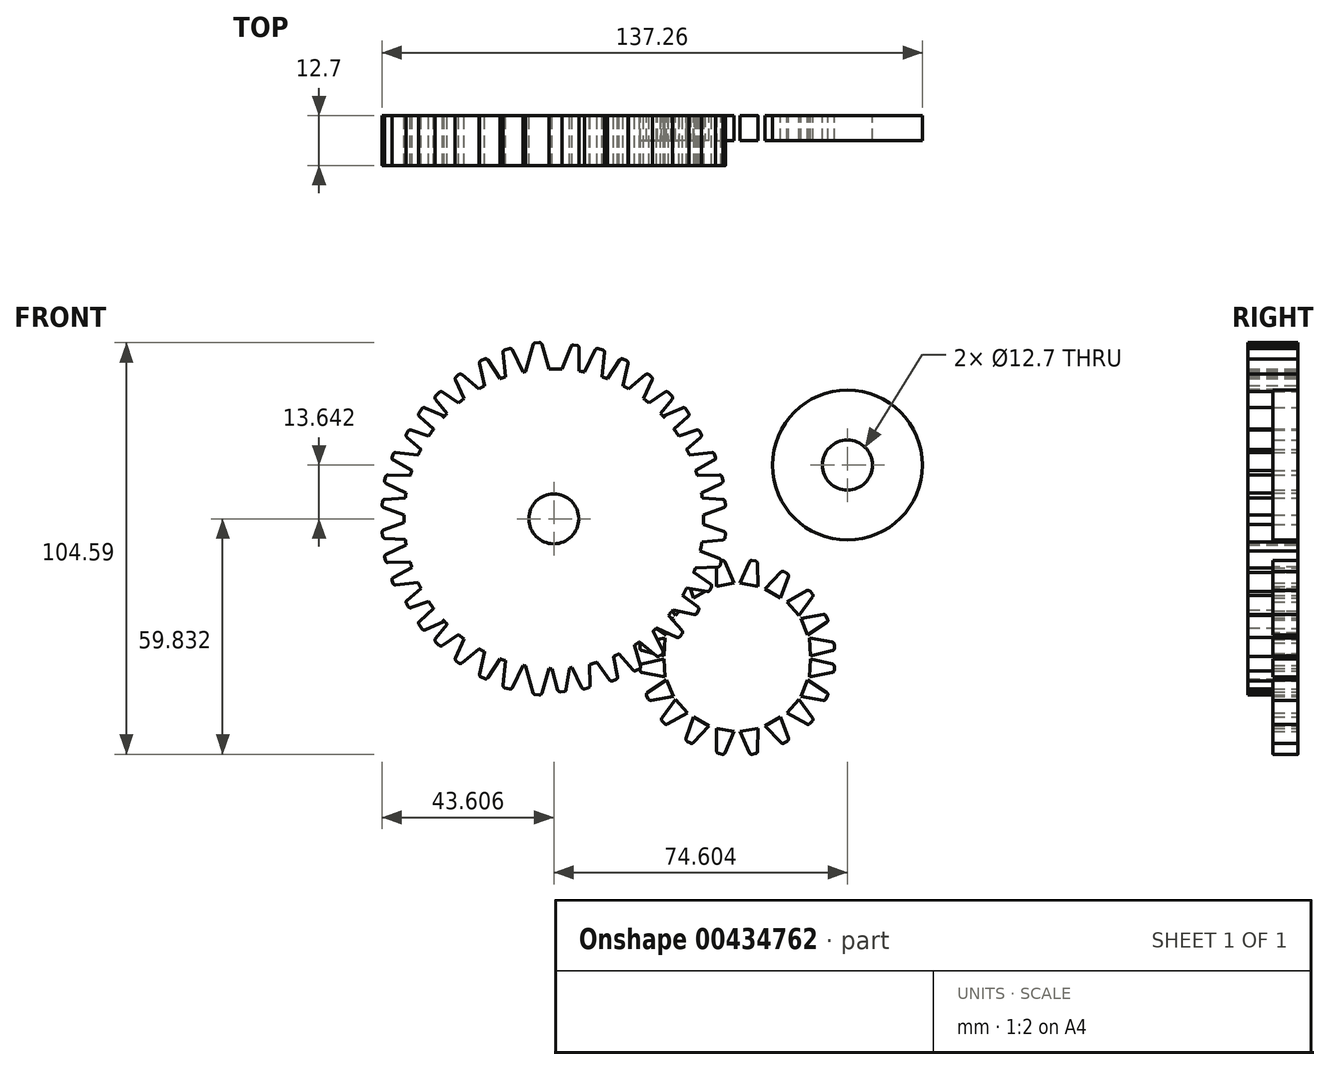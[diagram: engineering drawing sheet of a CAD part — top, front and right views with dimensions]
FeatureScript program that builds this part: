
annotation { "Feature Type Name" : "Feature", "Feature Type Description" : "" }
export const myFeature = defineFeature(function(context is Context, id is Id, definition is map)
    precondition{}
    {
        {
            var Q0;
            Q0=qCreatedBy(makeId("Front.planeOp"),FACE);
            var sketch = newSketch(context, id + "F0", { "sketchPlane" : qUnion([Q0])});
            skCircle(sketch, "E0", {"center": v(-46.58, 35.21) * mm, "radius": 38.1 * mm});
            skCircle(sketch, "E1", {"center": v(-46.58, 35.21) * mm, "radius": 6.35 * mm});
            skLineSegment(sketch, "E2", {"start": v(-46.58, -6.11) * mm, "end": v(-46.58, 81.19) * mm});
            skLineSegment(sketch, "E3", {"start": v(-89.25, 35.21) * mm, "end": v(4.56, 35.21) * mm});
            skSolve(sketch);
        }
        {
            var Q0;
            Q0 = qSketchRegion(id + "F0", true);
            extrude(context, id + "F1", {"entities" : qUnion([Q0]), "depth" : 12.7 * mm});
        }
        {
            var Q0;
            Q0=qCreatedBy(makeId("Front.planeOp"),FACE);
            var sketch = newSketch(context, id + "F2", { "sketchPlane" : qUnion([Q0])});
            skCircle(sketch, "E4", {"center": v(28.02, 48.85) * mm, "radius": 19.05 * mm});
            skCircle(sketch, "E5", {"center": v(28.02, 48.85) * mm, "radius": 6.35 * mm});
            skLineSegment(sketch, "E6", {"start": v(28.02, 28) * mm, "end": v(28.02, 72.6) * mm});
            skLineSegment(sketch, "E7", {"start": v(7.02, 48.85) * mm, "end": v(52.13, 48.85) * mm});
            skLineSegment(sketch, "E8", {"start": v(-5.28, 18.03) * mm, "end": v(-5.2, 23.83) * mm});
            skLineSegment(sketch, "E9", {"start": v(-4.68, 24.44) * mm, "end": v(-3.77, 24.6) * mm});
            skLineSegment(sketch, "E10", {"start": v(-3.08, 24.23) * mm, "end": v(-0.77, 18.85) * mm});
            skLineSegment(sketch, "E11", {"start": v(-5.28, 18.03) * mm, "end": v(-0.77, 18.85) * mm});
            skArc(sketch, "E12.filletArc", {"start": v(-4.68, 24.44) * mm, "mid": v(-5.05, 24.23) * mm, "end": v(-5.2, 23.83) * mm});
            skArc(sketch, "E13.filletArc", {"start": v(-3.08, 24.23) * mm, "mid": v(-3.36, 24.54) * mm, "end": v(-3.77, 24.6) * mm});
            skLineSegment(sketch, "E14.0", {"start": v(-5.28, 18.03) * mm, "end": v(-0.77, 18.85) * mm, "construction": true});
            skLineSegment(sketch, "E15", {"start": v(-11.07, 15.08) * mm, "end": v(-12.98, 20.55) * mm});
            skLineSegment(sketch, "E16", {"start": v(-12.7, 21.31) * mm, "end": v(-11.9, 21.78) * mm});
            skLineSegment(sketch, "E17", {"start": v(-11.12, 21.66) * mm, "end": v(-7.1, 17.4) * mm});
            skLineSegment(sketch, "E18", {"start": v(-11.07, 15.08) * mm, "end": v(-7.1, 17.4) * mm});
            skArc(sketch, "E19.filletArc", {"start": v(-12.7, 21.31) * mm, "mid": v(-12.97, 20.98) * mm, "end": v(-12.98, 20.55) * mm});
            skArc(sketch, "E20.filletArc", {"start": v(-11.12, 21.66) * mm, "mid": v(-11.5, 21.86) * mm, "end": v(-11.9, 21.78) * mm});
            skLineSegment(sketch, "E21.0", {"start": v(-11.07, 15.08) * mm, "end": v(-7.1, 17.4) * mm, "construction": true});
            skLineSegment(sketch, "E22", {"start": v(-18.58, 0.36) * mm, "end": v(-24.22, 1.72) * mm});
            skLineSegment(sketch, "E23", {"start": v(-24.7, 2.37) * mm, "end": v(-24.66, 3.28) * mm});
            skLineSegment(sketch, "E24", {"start": v(-24.15, 3.88) * mm, "end": v(-18.39, 4.95) * mm});
            skLineSegment(sketch, "E25", {"start": v(-18.58, 0.36) * mm, "end": v(-18.39, 4.95) * mm});
            skArc(sketch, "E26.filletArc", {"start": v(-24.7, 2.37) * mm, "mid": v(-24.58, 1.96) * mm, "end": v(-24.22, 1.72) * mm});
            skArc(sketch, "E27.filletArc", {"start": v(-24.15, 3.88) * mm, "mid": v(-24.5, 3.67) * mm, "end": v(-24.66, 3.28) * mm});
            skLineSegment(sketch, "E28.0", {"start": v(-18.58, 0.36) * mm, "end": v(-18.39, 4.95) * mm, "construction": true});
            skLineSegment(sketch, "E29", {"start": v(-17.91, 5.67) * mm, "end": v(-22.74, 8.88) * mm});
            skLineSegment(sketch, "E30", {"start": v(-22.98, 9.65) * mm, "end": v(-22.63, 10.5) * mm});
            skLineSegment(sketch, "E31", {"start": v(-21.93, 10.88) * mm, "end": v(-16.16, 9.91) * mm});
            skLineSegment(sketch, "E32", {"start": v(-17.91, 5.67) * mm, "end": v(-16.16, 9.91) * mm});
            skArc(sketch, "E33.filletArc", {"start": v(-22.98, 9.65) * mm, "mid": v(-23, 9.22) * mm, "end": v(-22.74, 8.88) * mm});
            skArc(sketch, "E34.filletArc", {"start": v(-21.93, 10.88) * mm, "mid": v(-22.35, 10.8) * mm, "end": v(-22.63, 10.5) * mm});
            skLineSegment(sketch, "E35.0", {"start": v(-17.91, 5.67) * mm, "end": v(-16.16, 9.91) * mm, "construction": true});
            skLineSegment(sketch, "E36", {"start": v(-15.7, 10.67) * mm, "end": v(-19.14, 15.34) * mm});
            skLineSegment(sketch, "E37", {"start": v(-19.1, 16.14) * mm, "end": v(-18.47, 16.82) * mm});
            skLineSegment(sketch, "E38", {"start": v(-17.7, 16.95) * mm, "end": v(-12.6, 14.06) * mm});
            skLineSegment(sketch, "E39", {"start": v(-15.7, 10.67) * mm, "end": v(-12.6, 14.06) * mm});
            skArc(sketch, "E40.filletArc", {"start": v(-19.1, 16.14) * mm, "mid": v(-19.26, 15.75) * mm, "end": v(-19.14, 15.34) * mm});
            skArc(sketch, "E41.filletArc", {"start": v(-17.7, 16.95) * mm, "mid": v(-18.1, 17.02) * mm, "end": v(-18.47, 16.82) * mm});
            skLineSegment(sketch, "E42.0", {"start": v(-15.7, 10.67) * mm, "end": v(-12.6, 14.06) * mm, "construction": true});
            skLineSegment(sketch, "E43.MirrorCS", {"start": v(5.28, 18.03) * mm, "end": v(0.77, 18.85) * mm, "construction": true});
            skLineSegment(sketch, "E44.MirrorCS", {"start": v(5.28, 18.03) * mm, "end": v(5.2, 23.83) * mm});
            skArc(sketch, "E45.MirrorCS", {"start": v(4.68, 24.44) * mm, "mid": v(5.05, 24.23) * mm, "end": v(5.2, 23.83) * mm});
            skLineSegment(sketch, "E46.MirrorCS", {"start": v(4.68, 24.44) * mm, "end": v(3.77, 24.6) * mm});
            skArc(sketch, "E47.MirrorCS", {"start": v(3.08, 24.23) * mm, "mid": v(3.36, 24.54) * mm, "end": v(3.77, 24.6) * mm});
            skLineSegment(sketch, "E48.MirrorCS", {"start": v(3.08, 24.23) * mm, "end": v(0.77, 18.85) * mm});
            skLineSegment(sketch, "E49.MirrorCS", {"start": v(11.07, 15.08) * mm, "end": v(7.1, 17.4) * mm, "construction": true});
            skLineSegment(sketch, "E50.MirrorCS", {"start": v(11.07, 15.08) * mm, "end": v(12.98, 20.55) * mm});
            skArc(sketch, "E51.MirrorCS", {"start": v(12.7, 21.31) * mm, "mid": v(12.97, 20.98) * mm, "end": v(12.98, 20.55) * mm});
            skLineSegment(sketch, "E52.MirrorCS", {"start": v(12.7, 21.31) * mm, "end": v(11.9, 21.78) * mm});
            skArc(sketch, "E53.MirrorCS", {"start": v(11.12, 21.66) * mm, "mid": v(11.5, 21.86) * mm, "end": v(11.9, 21.78) * mm});
            skLineSegment(sketch, "E54.MirrorCS", {"start": v(11.12, 21.66) * mm, "end": v(7.1, 17.4) * mm});
            skLineSegment(sketch, "E55.MirrorCS", {"start": v(15.7, 10.67) * mm, "end": v(12.6, 14.06) * mm, "construction": true});
            skLineSegment(sketch, "E56.MirrorCS", {"start": v(15.7, 10.67) * mm, "end": v(19.14, 15.34) * mm});
            skLineSegment(sketch, "E57.MirrorCS", {"start": v(19.1, 16.14) * mm, "end": v(18.47, 16.82) * mm});
            skArc(sketch, "E58.MirrorCS", {"start": v(17.7, 16.95) * mm, "mid": v(18.1, 17.02) * mm, "end": v(18.47, 16.82) * mm});
            skLineSegment(sketch, "E59.MirrorCS", {"start": v(17.7, 16.95) * mm, "end": v(12.6, 14.06) * mm});
            skLineSegment(sketch, "E60.MirrorCS", {"start": v(17.91, 5.67) * mm, "end": v(16.16, 9.91) * mm, "construction": true});
            skLineSegment(sketch, "E61.MirrorCS", {"start": v(17.91, 5.67) * mm, "end": v(22.74, 8.88) * mm});
            skArc(sketch, "E62.MirrorCS", {"start": v(22.98, 9.65) * mm, "mid": v(23, 9.22) * mm, "end": v(22.74, 8.88) * mm});
            skLineSegment(sketch, "E63.MirrorCS", {"start": v(22.98, 9.65) * mm, "end": v(22.63, 10.5) * mm});
            skArc(sketch, "E64.MirrorCS", {"start": v(21.93, 10.88) * mm, "mid": v(22.35, 10.8) * mm, "end": v(22.63, 10.5) * mm});
            skLineSegment(sketch, "E65.MirrorCS", {"start": v(21.93, 10.88) * mm, "end": v(16.16, 9.91) * mm});
            skArc(sketch, "E66.MirrorCS", {"start": v(19.1, 16.14) * mm, "mid": v(19.26, 15.75) * mm, "end": v(19.14, 15.34) * mm});
            skLineSegment(sketch, "E67.MirrorCS", {"start": v(18.58, 0.36) * mm, "end": v(18.39, 4.95) * mm, "construction": true});
            skLineSegment(sketch, "E68.MirrorCS", {"start": v(18.58, 0.36) * mm, "end": v(24.22, 1.72) * mm});
            skArc(sketch, "E69.MirrorCS", {"start": v(24.7, 2.37) * mm, "mid": v(24.58, 1.96) * mm, "end": v(24.22, 1.72) * mm});
            skLineSegment(sketch, "E70.MirrorCS", {"start": v(24.7, 2.37) * mm, "end": v(24.66, 3.28) * mm});
            skArc(sketch, "E71.MirrorCS", {"start": v(24.15, 3.88) * mm, "mid": v(24.5, 3.67) * mm, "end": v(24.66, 3.28) * mm});
            skLineSegment(sketch, "E72.MirrorCS", {"start": v(24.15, 3.88) * mm, "end": v(18.39, 4.95) * mm});
            skLineSegment(sketch, "E73.MirrorCS", {"start": v(5.28, -18.03) * mm, "end": v(0.77, -18.85) * mm, "construction": true});
            skLineSegment(sketch, "E74.MirrorCS", {"start": v(3.08, -24.23) * mm, "end": v(0.77, -18.85) * mm});
            skArc(sketch, "E75.MirrorCS", {"start": v(3.08, -24.23) * mm, "mid": v(3.36, -24.54) * mm, "end": v(3.77, -24.6) * mm});
            skLineSegment(sketch, "E76.MirrorCS", {"start": v(4.68, -24.44) * mm, "end": v(3.77, -24.6) * mm});
            skArc(sketch, "E77.MirrorCS", {"start": v(4.68, -24.44) * mm, "mid": v(5.05, -24.23) * mm, "end": v(5.2, -23.83) * mm});
            skLineSegment(sketch, "E78.MirrorCS", {"start": v(5.28, -18.03) * mm, "end": v(5.2, -23.83) * mm});
            skLineSegment(sketch, "E79.MirrorCS", {"start": v(11.07, -15.08) * mm, "end": v(7.1, -17.4) * mm, "construction": true});
            skLineSegment(sketch, "E80.MirrorCS", {"start": v(11.12, -21.66) * mm, "end": v(7.1, -17.4) * mm});
            skArc(sketch, "E81.MirrorCS", {"start": v(11.12, -21.66) * mm, "mid": v(11.5, -21.86) * mm, "end": v(11.9, -21.78) * mm});
            skLineSegment(sketch, "E82.MirrorCS", {"start": v(12.7, -21.31) * mm, "end": v(11.9, -21.78) * mm});
            skArc(sketch, "E83.MirrorCS", {"start": v(12.7, -21.31) * mm, "mid": v(12.97, -20.98) * mm, "end": v(12.98, -20.55) * mm});
            skLineSegment(sketch, "E84.MirrorCS", {"start": v(11.07, -15.08) * mm, "end": v(12.98, -20.55) * mm});
            skLineSegment(sketch, "E85.MirrorCS", {"start": v(15.7, -10.67) * mm, "end": v(12.6, -14.06) * mm, "construction": true});
            skLineSegment(sketch, "E86.MirrorCS", {"start": v(17.7, -16.95) * mm, "end": v(12.6, -14.06) * mm});
            skArc(sketch, "E87.MirrorCS", {"start": v(17.7, -16.95) * mm, "mid": v(18.1, -17.02) * mm, "end": v(18.47, -16.82) * mm});
            skLineSegment(sketch, "E88.MirrorCS", {"start": v(19.1, -16.14) * mm, "end": v(18.47, -16.82) * mm});
            skArc(sketch, "E89.MirrorCS", {"start": v(19.1, -16.14) * mm, "mid": v(19.26, -15.75) * mm, "end": v(19.14, -15.34) * mm});
            skLineSegment(sketch, "E90.MirrorCS", {"start": v(15.7, -10.67) * mm, "end": v(19.14, -15.34) * mm});
            skLineSegment(sketch, "E91.MirrorCS", {"start": v(17.91, -5.67) * mm, "end": v(16.16, -9.91) * mm, "construction": true});
            skLineSegment(sketch, "E92.MirrorCS", {"start": v(21.93, -10.88) * mm, "end": v(16.16, -9.91) * mm});
            skArc(sketch, "E93.MirrorCS", {"start": v(21.93, -10.88) * mm, "mid": v(22.35, -10.8) * mm, "end": v(22.63, -10.5) * mm});
            skLineSegment(sketch, "E94.MirrorCS", {"start": v(22.98, -9.65) * mm, "end": v(22.63, -10.5) * mm});
            skArc(sketch, "E95.MirrorCS", {"start": v(22.98, -9.65) * mm, "mid": v(23, -9.22) * mm, "end": v(22.74, -8.88) * mm});
            skLineSegment(sketch, "E96.MirrorCS", {"start": v(17.91, -5.67) * mm, "end": v(22.74, -8.88) * mm});
            skLineSegment(sketch, "E97.MirrorCS", {"start": v(18.58, -0.36) * mm, "end": v(18.39, -4.95) * mm, "construction": true});
            skLineSegment(sketch, "E98.MirrorCS", {"start": v(18.58, -0.36) * mm, "end": v(24.22, -1.72) * mm});
            skArc(sketch, "E99.MirrorCS", {"start": v(24.7, -2.37) * mm, "mid": v(24.58, -1.96) * mm, "end": v(24.22, -1.72) * mm});
            skLineSegment(sketch, "E100.MirrorCS", {"start": v(24.7, -2.37) * mm, "end": v(24.66, -3.28) * mm});
            skArc(sketch, "E101.MirrorCS", {"start": v(24.15, -3.88) * mm, "mid": v(24.5, -3.67) * mm, "end": v(24.66, -3.28) * mm});
            skLineSegment(sketch, "E102.MirrorCS", {"start": v(24.15, -3.88) * mm, "end": v(18.39, -4.95) * mm});
            skLineSegment(sketch, "E103.MirrorCS", {"start": v(-18.58, -0.36) * mm, "end": v(-24.22, -1.72) * mm});
            skArc(sketch, "E104.MirrorCS", {"start": v(-24.7, -2.37) * mm, "mid": v(-24.58, -1.96) * mm, "end": v(-24.22, -1.72) * mm});
            skLineSegment(sketch, "E105.MirrorCS", {"start": v(-24.7, -2.37) * mm, "end": v(-24.66, -3.28) * mm});
            skArc(sketch, "E106.MirrorCS", {"start": v(-24.15, -3.88) * mm, "mid": v(-24.5, -3.67) * mm, "end": v(-24.66, -3.28) * mm});
            skLineSegment(sketch, "E107.MirrorCS", {"start": v(-24.15, -3.88) * mm, "end": v(-18.39, -4.95) * mm});
            skLineSegment(sketch, "E108.MirrorCS", {"start": v(-18.58, -0.36) * mm, "end": v(-18.39, -4.95) * mm, "construction": true});
            skLineSegment(sketch, "E109.MirrorCS", {"start": v(-17.91, -5.67) * mm, "end": v(-16.16, -9.91) * mm, "construction": true});
            skLineSegment(sketch, "E110.MirrorCS", {"start": v(-17.91, -5.67) * mm, "end": v(-22.74, -8.88) * mm});
            skArc(sketch, "E111.MirrorCS", {"start": v(-22.98, -9.65) * mm, "mid": v(-23, -9.22) * mm, "end": v(-22.74, -8.88) * mm});
            skLineSegment(sketch, "E112.MirrorCS", {"start": v(-22.98, -9.65) * mm, "end": v(-22.63, -10.5) * mm});
            skArc(sketch, "E113.MirrorCS", {"start": v(-21.93, -10.88) * mm, "mid": v(-22.35, -10.8) * mm, "end": v(-22.63, -10.5) * mm});
            skLineSegment(sketch, "E114.MirrorCS", {"start": v(-21.93, -10.88) * mm, "end": v(-16.16, -9.91) * mm});
            skLineSegment(sketch, "E115.MirrorCS", {"start": v(-15.7, -10.67) * mm, "end": v(-12.6, -14.06) * mm, "construction": true});
            skLineSegment(sketch, "E116.MirrorCS", {"start": v(-15.7, -10.67) * mm, "end": v(-19.14, -15.34) * mm});
            skArc(sketch, "E117.MirrorCS", {"start": v(-19.1, -16.14) * mm, "mid": v(-19.26, -15.75) * mm, "end": v(-19.14, -15.34) * mm});
            skLineSegment(sketch, "E118.MirrorCS", {"start": v(-19.1, -16.14) * mm, "end": v(-18.47, -16.82) * mm});
            skArc(sketch, "E119.MirrorCS", {"start": v(-17.7, -16.95) * mm, "mid": v(-18.1, -17.02) * mm, "end": v(-18.47, -16.82) * mm});
            skLineSegment(sketch, "E120.MirrorCS", {"start": v(-17.7, -16.95) * mm, "end": v(-12.6, -14.06) * mm});
            skLineSegment(sketch, "E121.MirrorCS", {"start": v(-11.07, -15.08) * mm, "end": v(-7.1, -17.4) * mm, "construction": true});
            skLineSegment(sketch, "E122.MirrorCS", {"start": v(-11.07, -15.08) * mm, "end": v(-12.98, -20.55) * mm});
            skLineSegment(sketch, "E123.MirrorCS", {"start": v(-12.7, -21.31) * mm, "end": v(-11.9, -21.78) * mm});
            skArc(sketch, "E124.MirrorCS", {"start": v(-12.7, -21.31) * mm, "mid": v(-12.97, -20.98) * mm, "end": v(-12.98, -20.55) * mm});
            skArc(sketch, "E125.MirrorCS", {"start": v(-11.12, -21.66) * mm, "mid": v(-11.5, -21.86) * mm, "end": v(-11.9, -21.78) * mm});
            skLineSegment(sketch, "E126.MirrorCS", {"start": v(-11.12, -21.66) * mm, "end": v(-7.1, -17.4) * mm});
            skLineSegment(sketch, "E127.MirrorCS", {"start": v(-5.28, -18.03) * mm, "end": v(-0.77, -18.85) * mm, "construction": true});
            skLineSegment(sketch, "E128.MirrorCS", {"start": v(-5.28, -18.03) * mm, "end": v(-5.2, -23.83) * mm});
            skArc(sketch, "E129.MirrorCS", {"start": v(-4.68, -24.44) * mm, "mid": v(-5.05, -24.23) * mm, "end": v(-5.2, -23.83) * mm});
            skLineSegment(sketch, "E130.MirrorCS", {"start": v(-4.68, -24.44) * mm, "end": v(-3.77, -24.6) * mm});
            skArc(sketch, "E131.MirrorCS", {"start": v(-3.08, -24.23) * mm, "mid": v(-3.36, -24.54) * mm, "end": v(-3.77, -24.6) * mm});
            skLineSegment(sketch, "E132.MirrorCS", {"start": v(-3.08, -24.23) * mm, "end": v(-0.77, -18.85) * mm});
            skLineSegment(sketch, "E133", {"start": v(-18.39, -4.95) * mm, "end": v(-18.58, -0.36) * mm});
            skLineSegment(sketch, "E134", {"start": v(-16.16, -9.91) * mm, "end": v(-17.91, -5.67) * mm});
            skLineSegment(sketch, "E135", {"start": v(-12.6, -14.06) * mm, "end": v(-15.7, -10.67) * mm});
            skLineSegment(sketch, "E136", {"start": v(-7.1, -17.4) * mm, "end": v(-11.07, -15.08) * mm});
            skLineSegment(sketch, "E137", {"start": v(-0.77, -18.85) * mm, "end": v(-5.28, -18.03) * mm});
            skLineSegment(sketch, "E138", {"start": v(5.28, -18.03) * mm, "end": v(0.77, -18.85) * mm});
            skLineSegment(sketch, "E139", {"start": v(11.07, -15.08) * mm, "end": v(7.1, -17.4) * mm});
            skLineSegment(sketch, "E140", {"start": v(15.7, -10.67) * mm, "end": v(12.6, -14.06) * mm});
            skLineSegment(sketch, "E141", {"start": v(17.91, -5.67) * mm, "end": v(16.16, -9.91) * mm});
            skLineSegment(sketch, "E142", {"start": v(18.39, -4.95) * mm, "end": v(18.58, -0.36) * mm});
            skLineSegment(sketch, "E143", {"start": v(18.58, 0.36) * mm, "end": v(18.39, 4.95) * mm});
            skLineSegment(sketch, "E144", {"start": v(17.91, 5.67) * mm, "end": v(16.16, 9.91) * mm});
            skLineSegment(sketch, "E145", {"start": v(15.7, 10.67) * mm, "end": v(12.6, 14.06) * mm});
            skLineSegment(sketch, "E146", {"start": v(11.07, 15.08) * mm, "end": v(7.1, 17.4) * mm});
            skLineSegment(sketch, "E147", {"start": v(5.28, 18.03) * mm, "end": v(0.77, 18.85) * mm});
            skSolve(sketch);
        }
        {
            var Q0;
            Q0 = qSketchRegion(id + "F2", true);
            extrude(context, id + "F3", {"entities" : qUnion([Q0]), "depth" : 6.35 * mm});
        }
        {
            var Q0;
            Q0=qCreatedBy(makeId("Front.planeOp"),FACE);
            var sketch = newSketch(context, id + "F4", { "sketchPlane" : qUnion([Q0])});
            skLineSegment(sketch, "E148", {"start": v(-53.8, 72.63) * mm, "end": v(-51.9, 79.41) * mm});
            skLineSegment(sketch, "E149", {"start": v(-51.34, 79.87) * mm, "end": v(-50.28, 79.96) * mm});
            skLineSegment(sketch, "E150", {"start": v(-49.62, 79.5) * mm, "end": v(-47.8, 73.16) * mm});
            skLineSegment(sketch, "E151", {"start": v(-53.8, 72.63) * mm, "end": v(-47.8, 73.16) * mm});
            skPoint(sketch, "E152.visualSharp", {"position": v(-51.78, 79.83) * mm});
            skArc(sketch, "E152.filletArc", {"start": v(-51.34, 79.87) * mm, "mid": v(-51.7, 79.73) * mm, "end": v(-51.9, 79.41) * mm});
            skPoint(sketch, "E153.visualSharp", {"position": v(-49.76, 80.01) * mm});
            skArc(sketch, "E153.filletArc", {"start": v(-49.62, 79.5) * mm, "mid": v(-49.87, 79.86) * mm, "end": v(-50.28, 79.96) * mm});
            skLineSegment(sketch, "E154", {"start": v(-44.47, 73.21) * mm, "end": v(-42.23, 79) * mm});
            skLineSegment(sketch, "E155", {"start": v(-41.53, 79.4) * mm, "end": v(-40.69, 79.25) * mm});
            skLineSegment(sketch, "E156", {"start": v(-40.16, 78.63) * mm, "end": v(-40.16, 72.45) * mm});
            skLineSegment(sketch, "E157", {"start": v(-44.47, 73.21) * mm, "end": v(-40.16, 72.45) * mm});
            skArc(sketch, "E158.filletArc", {"start": v(-41.53, 79.4) * mm, "mid": v(-41.95, 79.33) * mm, "end": v(-42.23, 79) * mm});
            skArc(sketch, "E159.filletArc", {"start": v(-40.16, 78.63) * mm, "mid": v(-40.31, 79.04) * mm, "end": v(-40.69, 79.25) * mm});
            skLineSegment(sketch, "E160.0", {"start": v(-44.47, 73.21) * mm, "end": v(-40.16, 72.45) * mm, "construction": true});
            skLineSegment(sketch, "E161", {"start": v(-38.87, 72.35) * mm, "end": v(-36.07, 78.1) * mm});
            skLineSegment(sketch, "E162", {"start": v(-35.34, 78.44) * mm, "end": v(-34.13, 78.12) * mm});
            skLineSegment(sketch, "E163", {"start": v(-33.66, 77.44) * mm, "end": v(-34.37, 71.16) * mm});
            skLineSegment(sketch, "E164", {"start": v(-38.87, 72.35) * mm, "end": v(-34.37, 71.16) * mm});
            skArc(sketch, "E165.filletArc", {"start": v(-35.34, 78.44) * mm, "mid": v(-35.76, 78.4) * mm, "end": v(-36.07, 78.1) * mm});
            skArc(sketch, "E166.filletArc", {"start": v(-33.66, 77.44) * mm, "mid": v(-33.77, 77.87) * mm, "end": v(-34.13, 78.12) * mm});
            skLineSegment(sketch, "E167.0", {"start": v(-38.87, 72.35) * mm, "end": v(-34.37, 71.16) * mm, "construction": true});
            skLineSegment(sketch, "E168", {"start": v(-33.08, 70.6) * mm, "end": v(-29.83, 75.58) * mm});
            skLineSegment(sketch, "E169", {"start": v(-29.06, 75.82) * mm, "end": v(-28.14, 75.45) * mm});
            skLineSegment(sketch, "E170", {"start": v(-27.76, 74.73) * mm, "end": v(-29.04, 68.96) * mm});
            skLineSegment(sketch, "E171", {"start": v(-33.08, 70.6) * mm, "end": v(-29.04, 68.96) * mm});
            skArc(sketch, "E172.filletArc", {"start": v(-29.06, 75.82) * mm, "mid": v(-29.49, 75.84) * mm, "end": v(-29.83, 75.58) * mm});
            skArc(sketch, "E173.filletArc", {"start": v(-27.76, 74.73) * mm, "mid": v(-27.82, 75.16) * mm, "end": v(-28.14, 75.45) * mm});
            skLineSegment(sketch, "E174.0", {"start": v(-33.08, 70.6) * mm, "end": v(-29.04, 68.96) * mm, "construction": true});
            skLineSegment(sketch, "E175", {"start": v(-27.74, 68.12) * mm, "end": v(-23.24, 71.82) * mm});
            skLineSegment(sketch, "E176", {"start": v(-22.43, 71.82) * mm, "end": v(-21.78, 71.29) * mm});
            skLineSegment(sketch, "E177", {"start": v(-21.61, 70.53) * mm, "end": v(-24.06, 65.31) * mm});
            skLineSegment(sketch, "E178", {"start": v(-27.74, 68.12) * mm, "end": v(-24.06, 65.31) * mm});
            skArc(sketch, "E179.filletArc", {"start": v(-22.43, 71.82) * mm, "mid": v(-22.83, 71.97) * mm, "end": v(-23.24, 71.82) * mm});
            skArc(sketch, "E180.filletArc", {"start": v(-21.61, 70.53) * mm, "mid": v(-21.57, 70.94) * mm, "end": v(-21.78, 71.29) * mm});
            skLineSegment(sketch, "E181", {"start": v(-22.64, 64.39) * mm, "end": v(-18.3, 67.4) * mm});
            skLineSegment(sketch, "E182", {"start": v(-17.5, 67.33) * mm, "end": v(-16.58, 66.44) * mm});
            skLineSegment(sketch, "E183", {"start": v(-16.54, 65.58) * mm, "end": v(-19.82, 61.65) * mm});
            skLineSegment(sketch, "E184", {"start": v(-22.64, 64.39) * mm, "end": v(-19.82, 61.65) * mm});
            skArc(sketch, "E185.filletArc", {"start": v(-17.5, 67.33) * mm, "mid": v(-17.89, 67.5) * mm, "end": v(-18.3, 67.4) * mm});
            skArc(sketch, "E186.filletArc", {"start": v(-16.54, 65.58) * mm, "mid": v(-16.4, 66.02) * mm, "end": v(-16.58, 66.44) * mm});
            skLineSegment(sketch, "E187.0", {"start": v(-22.64, 64.39) * mm, "end": v(-19.82, 61.65) * mm, "construction": true});
            skLineSegment(sketch, "E188", {"start": v(-12.27, 51.4) * mm, "end": v(-6.43, 52.03) * mm});
            skLineSegment(sketch, "E189", {"start": v(-5.75, 51.59) * mm, "end": v(-5.52, 50.84) * mm});
            skLineSegment(sketch, "E190", {"start": v(-5.82, 50.1) * mm, "end": v(-11, 47.3) * mm});
            skLineSegment(sketch, "E191", {"start": v(-12.27, 51.4) * mm, "end": v(-11, 47.3) * mm});
            skArc(sketch, "E192.filletArc", {"start": v(-5.75, 51.59) * mm, "mid": v(-6.01, 51.93) * mm, "end": v(-6.43, 52.03) * mm});
            skArc(sketch, "E193.filletArc", {"start": v(-5.82, 50.1) * mm, "mid": v(-5.54, 50.41) * mm, "end": v(-5.52, 50.84) * mm});
            skLineSegment(sketch, "E194.0", {"start": v(-12.27, 51.4) * mm, "end": v(-11, 47.3) * mm, "construction": true});
            skLineSegment(sketch, "E195", {"start": v(-10.26, 46.18) * mm, "end": v(-4.47, 46.32) * mm});
            skLineSegment(sketch, "E196", {"start": v(-3.83, 45.83) * mm, "end": v(-3.63, 44.93) * mm});
            skLineSegment(sketch, "E197", {"start": v(-3.98, 44.22) * mm, "end": v(-9.27, 41.7) * mm});
            skLineSegment(sketch, "E198", {"start": v(-10.26, 46.18) * mm, "end": v(-9.27, 41.7) * mm});
            skArc(sketch, "E199.filletArc", {"start": v(-3.83, 45.83) * mm, "mid": v(-4.06, 46.2) * mm, "end": v(-4.47, 46.32) * mm});
            skArc(sketch, "E200.filletArc", {"start": v(-3.98, 44.22) * mm, "mid": v(-3.68, 44.52) * mm, "end": v(-3.63, 44.93) * mm});
            skLineSegment(sketch, "E201.0", {"start": v(-10.26, 46.18) * mm, "end": v(-9.27, 41.7) * mm, "construction": true});
            skLineSegment(sketch, "E202", {"start": v(-15.38, 56.07) * mm, "end": v(-10.36, 57.79) * mm});
            skLineSegment(sketch, "E203", {"start": v(-9.6, 57.5) * mm, "end": v(-9.15, 56.72) * mm});
            skLineSegment(sketch, "E204", {"start": v(-9.29, 55.93) * mm, "end": v(-13.62, 52.15) * mm});
            skLineSegment(sketch, "E205", {"start": v(-15.38, 56.07) * mm, "end": v(-13.62, 52.15) * mm});
            skArc(sketch, "E206.filletArc", {"start": v(-9.6, 57.5) * mm, "mid": v(-9.93, 57.78) * mm, "end": v(-10.36, 57.79) * mm});
            skArc(sketch, "E207.filletArc", {"start": v(-9.29, 55.93) * mm, "mid": v(-9.08, 56.3) * mm, "end": v(-9.15, 56.72) * mm});
            skLineSegment(sketch, "E208", {"start": v(-9.48, 40.53) * mm, "end": v(-3.7, 40.16) * mm});
            skLineSegment(sketch, "E209", {"start": v(-3.1, 39.61) * mm, "end": v(-2.99, 38.7) * mm});
            skLineSegment(sketch, "E210", {"start": v(-3.4, 38.02) * mm, "end": v(-8.88, 35.97) * mm});
            skLineSegment(sketch, "E211", {"start": v(-9.48, 40.53) * mm, "end": v(-8.88, 35.97) * mm});
            skArc(sketch, "E212.filletArc", {"start": v(-3.1, 39.61) * mm, "mid": v(-3.3, 40) * mm, "end": v(-3.7, 40.16) * mm});
            skArc(sketch, "E213.filletArc", {"start": v(-3.4, 38.02) * mm, "mid": v(-3.07, 38.3) * mm, "end": v(-2.99, 38.7) * mm});
            skLineSegment(sketch, "E214.0", {"start": v(-9.48, 40.53) * mm, "end": v(-8.88, 35.97) * mm, "construction": true});
            skLineSegment(sketch, "E215", {"start": v(-31.54, 0.77) * mm, "end": v(-30.39, -4.91) * mm});
            skLineSegment(sketch, "E216", {"start": v(-30.77, -5.62) * mm, "end": v(-31.62, -5.98) * mm});
            skLineSegment(sketch, "E217", {"start": v(-32.38, -5.76) * mm, "end": v(-35.78, -0.99) * mm});
            skLineSegment(sketch, "E218", {"start": v(-31.54, 0.77) * mm, "end": v(-35.78, -0.99) * mm});
            skArc(sketch, "E219.filletArc", {"start": v(-30.77, -5.62) * mm, "mid": v(-30.45, -5.34) * mm, "end": v(-30.39, -4.91) * mm});
            skArc(sketch, "E220.filletArc", {"start": v(-32.38, -5.76) * mm, "mid": v(-32.03, -6) * mm, "end": v(-31.62, -5.98) * mm});
            skLineSegment(sketch, "E221.0", {"start": v(-31.54, 0.77) * mm, "end": v(-35.78, -0.99) * mm, "construction": true});
            skLineSegment(sketch, "E222", {"start": v(-37.55, -1.37) * mm, "end": v(-37.4, -7.16) * mm});
            skLineSegment(sketch, "E223", {"start": v(-37.9, -7.8) * mm, "end": v(-38.8, -8) * mm});
            skLineSegment(sketch, "E224", {"start": v(-39.5, -7.65) * mm, "end": v(-42.03, -2.36) * mm});
            skLineSegment(sketch, "E225", {"start": v(-37.55, -1.37) * mm, "end": v(-42.03, -2.36) * mm});
            skArc(sketch, "E226.filletArc", {"start": v(-37.9, -7.8) * mm, "mid": v(-37.54, -7.57) * mm, "end": v(-37.4, -7.16) * mm});
            skArc(sketch, "E227.filletArc", {"start": v(-39.5, -7.65) * mm, "mid": v(-39.21, -7.95) * mm, "end": v(-38.8, -8) * mm});
            skLineSegment(sketch, "E228.0", {"start": v(-37.55, -1.37) * mm, "end": v(-42.03, -2.36) * mm, "construction": true});
            skLineSegment(sketch, "E229", {"start": v(-26.2, 3.38) * mm, "end": v(-24.55, -2.18) * mm});
            skLineSegment(sketch, "E230", {"start": v(-24.87, -2.93) * mm, "end": v(-25.68, -3.35) * mm});
            skLineSegment(sketch, "E231", {"start": v(-26.46, -3.2) * mm, "end": v(-30.26, 1.26) * mm});
            skLineSegment(sketch, "E232", {"start": v(-26.2, 3.38) * mm, "end": v(-30.26, 1.26) * mm});
            skArc(sketch, "E233.filletArc", {"start": v(-24.87, -2.93) * mm, "mid": v(-24.58, -2.61) * mm, "end": v(-24.55, -2.18) * mm});
            skArc(sketch, "E234.filletArc", {"start": v(-26.46, -3.2) * mm, "mid": v(-26.1, -3.41) * mm, "end": v(-25.68, -3.35) * mm});
            skLineSegment(sketch, "E235.0", {"start": v(-26.2, 3.38) * mm, "end": v(-30.26, 1.26) * mm, "construction": true});
            skLineSegment(sketch, "E236", {"start": v(-21.42, 6.87) * mm, "end": v(-18.84, 1.68) * mm});
            skLineSegment(sketch, "E237", {"start": v(-19.02, 0.9) * mm, "end": v(-19.75, 0.33) * mm});
            skLineSegment(sketch, "E238", {"start": v(-20.54, 0.35) * mm, "end": v(-25.06, 4.08) * mm});
            skLineSegment(sketch, "E239", {"start": v(-21.42, 6.87) * mm, "end": v(-25.06, 4.08) * mm});
            skArc(sketch, "E240.filletArc", {"start": v(-19.02, 0.9) * mm, "mid": v(-18.79, 1.25) * mm, "end": v(-18.84, 1.68) * mm});
            skArc(sketch, "E241.filletArc", {"start": v(-20.54, 0.35) * mm, "mid": v(-20.15, 0.2) * mm, "end": v(-19.75, 0.33) * mm});
            skLineSegment(sketch, "E242.0", {"start": v(-21.42, 6.87) * mm, "end": v(-25.06, 4.08) * mm, "construction": true});
            skLineSegment(sketch, "E243", {"start": v(-17.86, 11.17) * mm, "end": v(-14.03, 6.82) * mm});
            skLineSegment(sketch, "E244", {"start": v(-14, 6.02) * mm, "end": v(-14.56, 5.29) * mm});
            skLineSegment(sketch, "E245", {"start": v(-15.33, 5.1) * mm, "end": v(-20.65, 7.53) * mm});
            skLineSegment(sketch, "E246", {"start": v(-17.86, 11.17) * mm, "end": v(-20.65, 7.53) * mm});
            skArc(sketch, "E247.filletArc", {"start": v(-14, 6.02) * mm, "mid": v(-13.87, 6.42) * mm, "end": v(-14.03, 6.82) * mm});
            skArc(sketch, "E248.filletArc", {"start": v(-15.33, 5.1) * mm, "mid": v(-14.9, 5.06) * mm, "end": v(-14.56, 5.29) * mm});
            skLineSegment(sketch, "E249.0", {"start": v(-17.86, 11.17) * mm, "end": v(-20.65, 7.53) * mm, "construction": true});
            skLineSegment(sketch, "E250", {"start": v(-14.66, 16.28) * mm, "end": v(-10, 12.83) * mm});
            skLineSegment(sketch, "E251", {"start": v(-9.8, 12.05) * mm, "end": v(-10.2, 11.22) * mm});
            skLineSegment(sketch, "E252", {"start": v(-10.9, 10.87) * mm, "end": v(-16.63, 12.13) * mm});
            skLineSegment(sketch, "E253", {"start": v(-14.66, 16.28) * mm, "end": v(-16.63, 12.13) * mm});
            skArc(sketch, "E254.filletArc", {"start": v(-9.8, 12.05) * mm, "mid": v(-9.76, 12.48) * mm, "end": v(-10, 12.83) * mm});
            skArc(sketch, "E255.filletArc", {"start": v(-10.9, 10.87) * mm, "mid": v(-10.49, 10.92) * mm, "end": v(-10.2, 11.22) * mm});
            skLineSegment(sketch, "E256.0", {"start": v(-14.66, 16.28) * mm, "end": v(-16.63, 12.13) * mm, "construction": true});
            skLineSegment(sketch, "E257", {"start": v(-11.6, 21.91) * mm, "end": v(-6.78, 18.7) * mm});
            skLineSegment(sketch, "E258", {"start": v(-6.54, 17.93) * mm, "end": v(-6.9, 17.09) * mm});
            skLineSegment(sketch, "E259", {"start": v(-7.59, 16.7) * mm, "end": v(-13.36, 17.67) * mm});
            skLineSegment(sketch, "E260", {"start": v(-11.6, 21.91) * mm, "end": v(-13.36, 17.67) * mm});
            skArc(sketch, "E261.filletArc", {"start": v(-6.54, 17.93) * mm, "mid": v(-6.52, 18.36) * mm, "end": v(-6.78, 18.7) * mm});
            skArc(sketch, "E262.filletArc", {"start": v(-7.59, 16.7) * mm, "mid": v(-7.17, 16.77) * mm, "end": v(-6.9, 17.09) * mm});
            skLineSegment(sketch, "E263.0", {"start": v(-11.6, 21.91) * mm, "end": v(-13.36, 17.67) * mm, "construction": true});
            skLineSegment(sketch, "E264", {"start": v(-9.92, 27.21) * mm, "end": v(-4.52, 25.12) * mm});
            skLineSegment(sketch, "E265", {"start": v(-4.12, 24.42) * mm, "end": v(-4.28, 23.51) * mm});
            skLineSegment(sketch, "E266", {"start": v(-4.88, 23) * mm, "end": v(-10.73, 22.7) * mm});
            skLineSegment(sketch, "E267", {"start": v(-9.92, 27.21) * mm, "end": v(-10.73, 22.7) * mm});
            skArc(sketch, "E268.filletArc", {"start": v(-4.12, 24.42) * mm, "mid": v(-4.2, 24.84) * mm, "end": v(-4.52, 25.12) * mm});
            skArc(sketch, "E269.filletArc", {"start": v(-4.88, 23) * mm, "mid": v(-4.49, 23.15) * mm, "end": v(-4.28, 23.51) * mm});
            skLineSegment(sketch, "E270.0", {"start": v(-9.92, 27.21) * mm, "end": v(-10.73, 22.7) * mm, "construction": true});
            skLineSegment(sketch, "E271", {"start": v(-8.89, 33.84) * mm, "end": v(-3.4, 32) * mm});
            skLineSegment(sketch, "E272", {"start": v(-2.97, 31.31) * mm, "end": v(-3.09, 30.4) * mm});
            skLineSegment(sketch, "E273", {"start": v(-3.66, 29.85) * mm, "end": v(-9.49, 29.3) * mm});
            skLineSegment(sketch, "E274", {"start": v(-8.89, 33.84) * mm, "end": v(-9.49, 29.3) * mm});
            skArc(sketch, "E275.filletArc", {"start": v(-2.97, 31.31) * mm, "mid": v(-3.06, 31.73) * mm, "end": v(-3.4, 32) * mm});
            skArc(sketch, "E276.filletArc", {"start": v(-3.66, 29.85) * mm, "mid": v(-3.27, 30.03) * mm, "end": v(-3.09, 30.4) * mm});
            skLineSegment(sketch, "E277.0", {"start": v(-8.89, 33.84) * mm, "end": v(-9.49, 29.3) * mm, "construction": true});
            skLineSegment(sketch, "E278.0", {"start": v(-53.8, 72.63) * mm, "end": v(-47.8, 73.16) * mm, "construction": true});
            skLineSegment(sketch, "E279", {"start": v(-18.7, 61.28) * mm, "end": v(-13.87, 63.4) * mm});
            skLineSegment(sketch, "E280", {"start": v(-13.1, 63.18) * mm, "end": v(-12.33, 62.08) * mm});
            skLineSegment(sketch, "E281", {"start": v(-12.43, 61.24) * mm, "end": v(-16.3, 57.82) * mm});
            skLineSegment(sketch, "E282", {"start": v(-18.7, 61.28) * mm, "end": v(-16.3, 57.82) * mm});
            skArc(sketch, "E283.filletArc", {"start": v(-13.1, 63.18) * mm, "mid": v(-13.44, 63.43) * mm, "end": v(-13.87, 63.4) * mm});
            skArc(sketch, "E284.filletArc", {"start": v(-12.43, 61.24) * mm, "mid": v(-12.22, 61.64) * mm, "end": v(-12.33, 62.08) * mm});
            skLineSegment(sketch, "E285.0", {"start": v(-18.7, 61.28) * mm, "end": v(-16.3, 57.82) * mm, "construction": true});
            skLineSegment(sketch, "E286.MirrorCS", {"start": v(-54.3, 72.35) * mm, "end": v(-57.1, 78.1) * mm});
            skLineSegment(sketch, "E287.MirrorCS", {"start": v(-54.3, 72.35) * mm, "end": v(-58.8, 71.16) * mm, "construction": true});
            skLineSegment(sketch, "E288.MirrorCS", {"start": v(-59.5, 77.44) * mm, "end": v(-58.8, 71.16) * mm});
            skLineSegment(sketch, "E289.MirrorCS", {"start": v(-57.83, 78.44) * mm, "end": v(-59.04, 78.12) * mm});
            skArc(sketch, "E290.MirrorCS", {"start": v(-57.83, 78.44) * mm, "mid": v(-57.4, 78.4) * mm, "end": v(-57.1, 78.1) * mm});
            skArc(sketch, "E291.MirrorCS", {"start": v(-59.5, 77.44) * mm, "mid": v(-59.4, 77.87) * mm, "end": v(-59.04, 78.12) * mm});
            skLineSegment(sketch, "E292.MirrorCS", {"start": v(-60.09, 70.6) * mm, "end": v(-64.13, 68.96) * mm, "construction": true});
            skLineSegment(sketch, "E293.MirrorCS", {"start": v(-65.4, 74.73) * mm, "end": v(-64.13, 68.96) * mm});
            skArc(sketch, "E294.MirrorCS", {"start": v(-65.4, 74.73) * mm, "mid": v(-65.35, 75.16) * mm, "end": v(-65.03, 75.45) * mm});
            skLineSegment(sketch, "E295.MirrorCS", {"start": v(-64.11, 75.82) * mm, "end": v(-65.03, 75.45) * mm});
            skArc(sketch, "E296.MirrorCS", {"start": v(-64.11, 75.82) * mm, "mid": v(-63.68, 75.84) * mm, "end": v(-63.34, 75.58) * mm});
            skLineSegment(sketch, "E297.MirrorCS", {"start": v(-65.43, 68.12) * mm, "end": v(-69.93, 71.82) * mm});
            skLineSegment(sketch, "E298.MirrorCS", {"start": v(-71.56, 70.53) * mm, "end": v(-69.1, 65.31) * mm});
            skLineSegment(sketch, "E299.MirrorCS", {"start": v(-60.09, 70.6) * mm, "end": v(-63.34, 75.58) * mm});
            skLineSegment(sketch, "E300.MirrorCS", {"start": v(-65.43, 68.12) * mm, "end": v(-69.1, 65.31) * mm});
            skLineSegment(sketch, "E301.MirrorCS", {"start": v(-70.74, 71.82) * mm, "end": v(-71.39, 71.29) * mm});
            skArc(sketch, "E302.MirrorCS", {"start": v(-71.56, 70.53) * mm, "mid": v(-71.6, 70.94) * mm, "end": v(-71.39, 71.29) * mm});
            skArc(sketch, "E303.MirrorCS", {"start": v(-70.74, 71.82) * mm, "mid": v(-70.33, 71.97) * mm, "end": v(-69.93, 71.82) * mm});
            skLineSegment(sketch, "E304.MirrorCS", {"start": v(-76.63, 65.58) * mm, "end": v(-73.35, 61.65) * mm});
            skLineSegment(sketch, "E305.MirrorCS", {"start": v(-70.53, 64.39) * mm, "end": v(-73.35, 61.65) * mm, "construction": true});
            skLineSegment(sketch, "E306.MirrorCS", {"start": v(-70.53, 64.39) * mm, "end": v(-74.87, 67.4) * mm});
            skLineSegment(sketch, "E307.MirrorCS", {"start": v(-75.67, 67.33) * mm, "end": v(-76.58, 66.44) * mm});
            skArc(sketch, "E308.MirrorCS", {"start": v(-75.67, 67.33) * mm, "mid": v(-75.28, 67.5) * mm, "end": v(-74.87, 67.4) * mm});
            skArc(sketch, "E309.MirrorCS", {"start": v(-76.63, 65.58) * mm, "mid": v(-76.78, 66.02) * mm, "end": v(-76.58, 66.44) * mm});
            skLineSegment(sketch, "E310.MirrorCS", {"start": v(-74.48, 61.28) * mm, "end": v(-76.88, 57.82) * mm, "construction": true});
            skLineSegment(sketch, "E311.MirrorCS", {"start": v(-74.48, 61.28) * mm, "end": v(-79.3, 63.4) * mm});
            skArc(sketch, "E312.MirrorCS", {"start": v(-80.08, 63.18) * mm, "mid": v(-79.73, 63.43) * mm, "end": v(-79.3, 63.4) * mm});
            skLineSegment(sketch, "E313.MirrorCS", {"start": v(-80.08, 63.18) * mm, "end": v(-80.84, 62.08) * mm});
            skArc(sketch, "E314.MirrorCS", {"start": v(-80.74, 61.24) * mm, "mid": v(-80.95, 61.64) * mm, "end": v(-80.84, 62.08) * mm});
            skLineSegment(sketch, "E315.MirrorCS", {"start": v(-80.74, 61.24) * mm, "end": v(-76.88, 57.82) * mm});
            skLineSegment(sketch, "E316.MirrorCS", {"start": v(-83.88, 55.93) * mm, "end": v(-79.55, 52.15) * mm});
            skLineSegment(sketch, "E317.MirrorCS", {"start": v(-77.8, 56.07) * mm, "end": v(-79.55, 52.15) * mm});
            skLineSegment(sketch, "E318.MirrorCS", {"start": v(-77.8, 56.07) * mm, "end": v(-82.8, 57.79) * mm});
            skArc(sketch, "E319.MirrorCS", {"start": v(-83.56, 57.5) * mm, "mid": v(-83.23, 57.78) * mm, "end": v(-82.8, 57.79) * mm});
            skLineSegment(sketch, "E320.MirrorCS", {"start": v(-83.56, 57.5) * mm, "end": v(-84.01, 56.72) * mm});
            skArc(sketch, "E321.MirrorCS", {"start": v(-83.88, 55.93) * mm, "mid": v(-84.1, 56.3) * mm, "end": v(-84.01, 56.72) * mm});
            skLineSegment(sketch, "E322.MirrorCS", {"start": v(-87.34, 50.1) * mm, "end": v(-82.18, 47.3) * mm});
            skLineSegment(sketch, "E323.MirrorCS", {"start": v(-80.9, 51.4) * mm, "end": v(-86.74, 52.03) * mm});
            skLineSegment(sketch, "E324.MirrorCS", {"start": v(-80.9, 51.4) * mm, "end": v(-82.18, 47.3) * mm, "construction": true});
            skLineSegment(sketch, "E325.MirrorCS", {"start": v(-87.41, 51.59) * mm, "end": v(-87.65, 50.84) * mm});
            skArc(sketch, "E326.MirrorCS", {"start": v(-87.41, 51.59) * mm, "mid": v(-87.16, 51.93) * mm, "end": v(-86.74, 52.03) * mm});
            skArc(sketch, "E327.MirrorCS", {"start": v(-87.34, 50.1) * mm, "mid": v(-87.63, 50.41) * mm, "end": v(-87.65, 50.84) * mm});
            skLineSegment(sketch, "E328.MirrorCS", {"start": v(-89.19, 44.22) * mm, "end": v(-83.9, 41.7) * mm});
            skLineSegment(sketch, "E329.MirrorCS", {"start": v(-82.9, 46.18) * mm, "end": v(-83.9, 41.7) * mm, "construction": true});
            skLineSegment(sketch, "E330.MirrorCS", {"start": v(-82.9, 46.18) * mm, "end": v(-88.7, 46.32) * mm});
            skArc(sketch, "E331.MirrorCS", {"start": v(-89.34, 45.83) * mm, "mid": v(-89.1, 46.2) * mm, "end": v(-88.7, 46.32) * mm});
            skLineSegment(sketch, "E332.MirrorCS", {"start": v(-89.34, 45.83) * mm, "end": v(-89.53, 44.93) * mm});
            skArc(sketch, "E333.MirrorCS", {"start": v(-89.19, 44.22) * mm, "mid": v(-89.49, 44.52) * mm, "end": v(-89.53, 44.93) * mm});
            skLineSegment(sketch, "E334.MirrorCS", {"start": v(-83.69, 40.53) * mm, "end": v(-89.47, 40.16) * mm});
            skLineSegment(sketch, "E335.MirrorCS", {"start": v(-83.69, 40.53) * mm, "end": v(-84.29, 35.97) * mm, "construction": true});
            skLineSegment(sketch, "E336.MirrorCS", {"start": v(-89.77, 38.02) * mm, "end": v(-84.29, 35.97) * mm});
            skArc(sketch, "E337.MirrorCS", {"start": v(-89.77, 38.02) * mm, "mid": v(-90.1, 38.3) * mm, "end": v(-90.18, 38.7) * mm});
            skLineSegment(sketch, "E338.MirrorCS", {"start": v(-90.06, 39.61) * mm, "end": v(-90.18, 38.7) * mm});
            skArc(sketch, "E339.MirrorCS", {"start": v(-90.06, 39.61) * mm, "mid": v(-89.86, 40) * mm, "end": v(-89.47, 40.16) * mm});
            skLineSegment(sketch, "E340.MirrorCS", {"start": v(-89.77, 32.4) * mm, "end": v(-84.29, 34.45) * mm});
            skLineSegment(sketch, "E341.MirrorCS", {"start": v(-83.69, 29.9) * mm, "end": v(-84.29, 34.45) * mm, "construction": true});
            skLineSegment(sketch, "E342.MirrorCS", {"start": v(-83.69, 29.9) * mm, "end": v(-89.47, 30.26) * mm});
            skLineSegment(sketch, "E343.MirrorCS", {"start": v(-90.06, 30.81) * mm, "end": v(-90.18, 31.72) * mm});
            skArc(sketch, "E344.MirrorCS", {"start": v(-89.77, 32.4) * mm, "mid": v(-90.1, 32.13) * mm, "end": v(-90.18, 31.72) * mm});
            skArc(sketch, "E345.MirrorCS", {"start": v(-90.06, 30.81) * mm, "mid": v(-89.86, 30.43) * mm, "end": v(-89.47, 30.26) * mm});
            skLineSegment(sketch, "E346.MirrorCS", {"start": v(-89.19, 26.2) * mm, "end": v(-83.9, 28.72) * mm});
            skLineSegment(sketch, "E347.MirrorCS", {"start": v(-82.9, 24.24) * mm, "end": v(-83.9, 28.72) * mm, "construction": true});
            skLineSegment(sketch, "E348.MirrorCS", {"start": v(-82.9, 24.24) * mm, "end": v(-88.7, 24.1) * mm});
            skLineSegment(sketch, "E349.MirrorCS", {"start": v(-89.34, 24.6) * mm, "end": v(-89.53, 25.5) * mm});
            skArc(sketch, "E350.MirrorCS", {"start": v(-89.19, 26.2) * mm, "mid": v(-89.49, 25.9) * mm, "end": v(-89.53, 25.5) * mm});
            skArc(sketch, "E351.MirrorCS", {"start": v(-89.34, 24.6) * mm, "mid": v(-89.1, 24.23) * mm, "end": v(-88.7, 24.1) * mm});
            skLineSegment(sketch, "E352.MirrorCS", {"start": v(-87.34, 20.33) * mm, "end": v(-82.18, 23.13) * mm});
            skLineSegment(sketch, "E353.MirrorCS", {"start": v(-80.9, 19.03) * mm, "end": v(-82.18, 23.13) * mm, "construction": true});
            skLineSegment(sketch, "E354.MirrorCS", {"start": v(-80.9, 19.03) * mm, "end": v(-86.74, 18.4) * mm});
            skLineSegment(sketch, "E355.MirrorCS", {"start": v(-87.41, 18.84) * mm, "end": v(-87.65, 19.58) * mm});
            skArc(sketch, "E356.MirrorCS", {"start": v(-87.41, 18.84) * mm, "mid": v(-87.16, 18.5) * mm, "end": v(-86.74, 18.4) * mm});
            skLineSegment(sketch, "E357.MirrorCS", {"start": v(-77.8, 14.35) * mm, "end": v(-79.55, 18.27) * mm});
            skLineSegment(sketch, "E358.MirrorCS", {"start": v(-77.8, 14.35) * mm, "end": v(-82.8, 12.63) * mm});
            skLineSegment(sketch, "E359.MirrorCS", {"start": v(-83.88, 14.5) * mm, "end": v(-79.55, 18.27) * mm});
            skArc(sketch, "E360.MirrorCS", {"start": v(-83.88, 14.5) * mm, "mid": v(-84.1, 14.12) * mm, "end": v(-84.01, 13.7) * mm});
            skLineSegment(sketch, "E361.MirrorCS", {"start": v(-83.56, 12.92) * mm, "end": v(-84.01, 13.7) * mm});
            skArc(sketch, "E362.MirrorCS", {"start": v(-83.56, 12.92) * mm, "mid": v(-83.23, 12.64) * mm, "end": v(-82.8, 12.63) * mm});
            skLineSegment(sketch, "E363.MirrorCS", {"start": v(-74.48, 9.14) * mm, "end": v(-76.88, 12.6) * mm, "construction": true});
            skLineSegment(sketch, "E364.MirrorCS", {"start": v(-74.48, 9.14) * mm, "end": v(-79.3, 7.03) * mm});
            skArc(sketch, "E365.MirrorCS", {"start": v(-80.08, 7.25) * mm, "mid": v(-79.73, 7) * mm, "end": v(-79.3, 7.03) * mm});
            skLineSegment(sketch, "E366.MirrorCS", {"start": v(-80.08, 7.25) * mm, "end": v(-80.84, 8.34) * mm});
            skArc(sketch, "E367.MirrorCS", {"start": v(-80.74, 9.18) * mm, "mid": v(-80.95, 8.78) * mm, "end": v(-80.84, 8.34) * mm});
            skLineSegment(sketch, "E368.MirrorCS", {"start": v(-80.74, 9.18) * mm, "end": v(-76.88, 12.6) * mm});
            skLineSegment(sketch, "E369.MirrorCS", {"start": v(-70.53, 6.04) * mm, "end": v(-73.35, 8.78) * mm, "construction": true});
            skLineSegment(sketch, "E370.MirrorCS", {"start": v(-76.63, 4.84) * mm, "end": v(-73.35, 8.78) * mm});
            skArc(sketch, "E371.MirrorCS", {"start": v(-76.63, 4.84) * mm, "mid": v(-76.78, 4.4) * mm, "end": v(-76.58, 3.98) * mm});
            skLineSegment(sketch, "E372.MirrorCS", {"start": v(-75.67, 3.1) * mm, "end": v(-76.58, 3.98) * mm});
            skArc(sketch, "E373.MirrorCS", {"start": v(-75.67, 3.1) * mm, "mid": v(-75.28, 2.92) * mm, "end": v(-74.87, 3.03) * mm});
            skLineSegment(sketch, "E374.MirrorCS", {"start": v(-70.53, 6.04) * mm, "end": v(-74.87, 3.03) * mm});
            skLineSegment(sketch, "E375.MirrorCS", {"start": v(-65.43, 2.3) * mm, "end": v(-69.1, 5.11) * mm});
            skLineSegment(sketch, "E376.MirrorCS", {"start": v(-65.43, 2.3) * mm, "end": v(-69.93, -1.4) * mm});
            skLineSegment(sketch, "E377.MirrorCS", {"start": v(-71.56, -0.1) * mm, "end": v(-69.1, 5.11) * mm});
            skArc(sketch, "E378.MirrorCS", {"start": v(-71.56, -0.1) * mm, "mid": v(-71.6, -0.51) * mm, "end": v(-71.39, -0.86) * mm});
            skLineSegment(sketch, "E379.MirrorCS", {"start": v(-70.74, -1.4) * mm, "end": v(-71.39, -0.86) * mm});
            skArc(sketch, "E380.MirrorCS", {"start": v(-70.74, -1.4) * mm, "mid": v(-70.33, -1.54) * mm, "end": v(-69.93, -1.4) * mm});
            skLineSegment(sketch, "E381.MirrorCS", {"start": v(-60.09, -0.18) * mm, "end": v(-64.13, 1.46) * mm, "construction": true});
            skLineSegment(sketch, "E382.MirrorCS", {"start": v(-65.4, -4.3) * mm, "end": v(-64.13, 1.46) * mm});
            skArc(sketch, "E383.MirrorCS", {"start": v(-65.4, -4.3) * mm, "mid": v(-65.35, -4.73) * mm, "end": v(-65.03, -5.03) * mm});
            skLineSegment(sketch, "E384.MirrorCS", {"start": v(-64.11, -5.4) * mm, "end": v(-65.03, -5.03) * mm});
            skArc(sketch, "E385.MirrorCS", {"start": v(-64.11, -5.4) * mm, "mid": v(-63.68, -5.42) * mm, "end": v(-63.34, -5.16) * mm});
            skLineSegment(sketch, "E386.MirrorCS", {"start": v(-60.09, -0.18) * mm, "end": v(-63.34, -5.16) * mm});
            skLineSegment(sketch, "E387.MirrorCS", {"start": v(-59.5, -7.01) * mm, "end": v(-58.8, -0.74) * mm});
            skLineSegment(sketch, "E388.MirrorCS", {"start": v(-54.3, -1.93) * mm, "end": v(-58.8, -0.74) * mm, "construction": true});
            skLineSegment(sketch, "E389.MirrorCS", {"start": v(-54.3, -1.93) * mm, "end": v(-57.1, -7.68) * mm});
            skLineSegment(sketch, "E390.MirrorCS", {"start": v(-57.83, -8.02) * mm, "end": v(-59.04, -7.7) * mm});
            skArc(sketch, "E391.MirrorCS", {"start": v(-59.5, -7.01) * mm, "mid": v(-59.4, -7.44) * mm, "end": v(-59.04, -7.7) * mm});
            skArc(sketch, "E392.MirrorCS", {"start": v(-57.83, -8.02) * mm, "mid": v(-57.4, -7.98) * mm, "end": v(-57.1, -7.68) * mm});
            skLineSegment(sketch, "E393.MirrorCS", {"start": v(-53.8, -2.21) * mm, "end": v(-51.9, -8.99) * mm});
            skLineSegment(sketch, "E394.MirrorCS", {"start": v(-53.8, -2.21) * mm, "end": v(-47.8, -2.74) * mm, "construction": true});
            skLineSegment(sketch, "E395.MirrorCS", {"start": v(-49.62, -9.08) * mm, "end": v(-47.8, -2.74) * mm});
            skLineSegment(sketch, "E396.MirrorCS", {"start": v(-51.34, -9.45) * mm, "end": v(-50.28, -9.54) * mm});
            skArc(sketch, "E397.MirrorCS", {"start": v(-49.62, -9.08) * mm, "mid": v(-49.87, -9.43) * mm, "end": v(-50.28, -9.54) * mm});
            skArc(sketch, "E398.MirrorCS", {"start": v(-51.34, -9.45) * mm, "mid": v(-51.7, -9.3) * mm, "end": v(-51.9, -8.99) * mm});
            skLineSegment(sketch, "E399", {"start": v(-42.55, -2.42) * mm, "end": v(-43.42, -8.15) * mm});
            skLineSegment(sketch, "E400", {"start": v(-44.02, -8.69) * mm, "end": v(-44.93, -8.73) * mm});
            skLineSegment(sketch, "E401", {"start": v(-45.57, -8.26) * mm, "end": v(-47.14, -2.62) * mm});
            skLineSegment(sketch, "E402", {"start": v(-42.55, -2.42) * mm, "end": v(-47.14, -2.62) * mm});
            skArc(sketch, "E403.filletArc", {"start": v(-44.02, -8.69) * mm, "mid": v(-43.62, -8.52) * mm, "end": v(-43.42, -8.15) * mm});
            skArc(sketch, "E404.filletArc", {"start": v(-45.57, -8.26) * mm, "mid": v(-45.34, -8.6) * mm, "end": v(-44.93, -8.73) * mm});
            skLineSegment(sketch, "E405.0", {"start": v(-42.55, -2.42) * mm, "end": v(-47.14, -2.62) * mm, "construction": true});
            skLineSegment(sketch, "E406", {"start": v(-58.8, 71.16) * mm, "end": v(-54.3, 72.35) * mm});
            skLineSegment(sketch, "E407", {"start": v(-64.13, 68.96) * mm, "end": v(-60.09, 70.6) * mm});
            skLineSegment(sketch, "E408", {"start": v(-73.35, 61.65) * mm, "end": v(-70.53, 64.39) * mm});
            skLineSegment(sketch, "E409", {"start": v(-76.88, 57.82) * mm, "end": v(-74.48, 61.28) * mm});
            skLineSegment(sketch, "E410", {"start": v(-82.18, 47.3) * mm, "end": v(-80.9, 51.4) * mm});
            skLineSegment(sketch, "E411", {"start": v(-83.9, 41.7) * mm, "end": v(-82.9, 46.18) * mm});
            skLineSegment(sketch, "E412", {"start": v(-84.29, 35.97) * mm, "end": v(-83.69, 40.53) * mm});
            skLineSegment(sketch, "E413", {"start": v(-83.69, 29.9) * mm, "end": v(-84.29, 34.45) * mm});
            skLineSegment(sketch, "E414", {"start": v(-82.9, 24.24) * mm, "end": v(-83.9, 28.72) * mm});
            skLineSegment(sketch, "E415", {"start": v(-80.9, 19.03) * mm, "end": v(-82.18, 23.13) * mm});
            skLineSegment(sketch, "E416", {"start": v(-74.48, 9.14) * mm, "end": v(-76.88, 12.6) * mm});
            skLineSegment(sketch, "E417", {"start": v(-70.53, 6.04) * mm, "end": v(-73.35, 8.78) * mm});
            skLineSegment(sketch, "E418", {"start": v(-60.09, -0.18) * mm, "end": v(-64.13, 1.46) * mm});
            skLineSegment(sketch, "E419", {"start": v(-58.8, -0.74) * mm, "end": v(-54.3, -1.93) * mm});
            skLineSegment(sketch, "E420", {"start": v(-53.8, -2.21) * mm, "end": v(-47.8, -2.74) * mm});
            skArc(sketch, "E421.MirrorCS", {"start": v(-87.34, 20.33) * mm, "mid": v(-87.63, 20.01) * mm, "end": v(-87.65, 19.58) * mm});
            skSolve(sketch);
        }
        {
            var Q0;
            Q0 = qSketchRegion(id + "F4", true);
            extrude(context, id + "F5", {"entities" : qUnion([Q0]), "operationType" : NewBodyOperationType.ADD, "depth" : 12.7 * mm});
        }
    });
